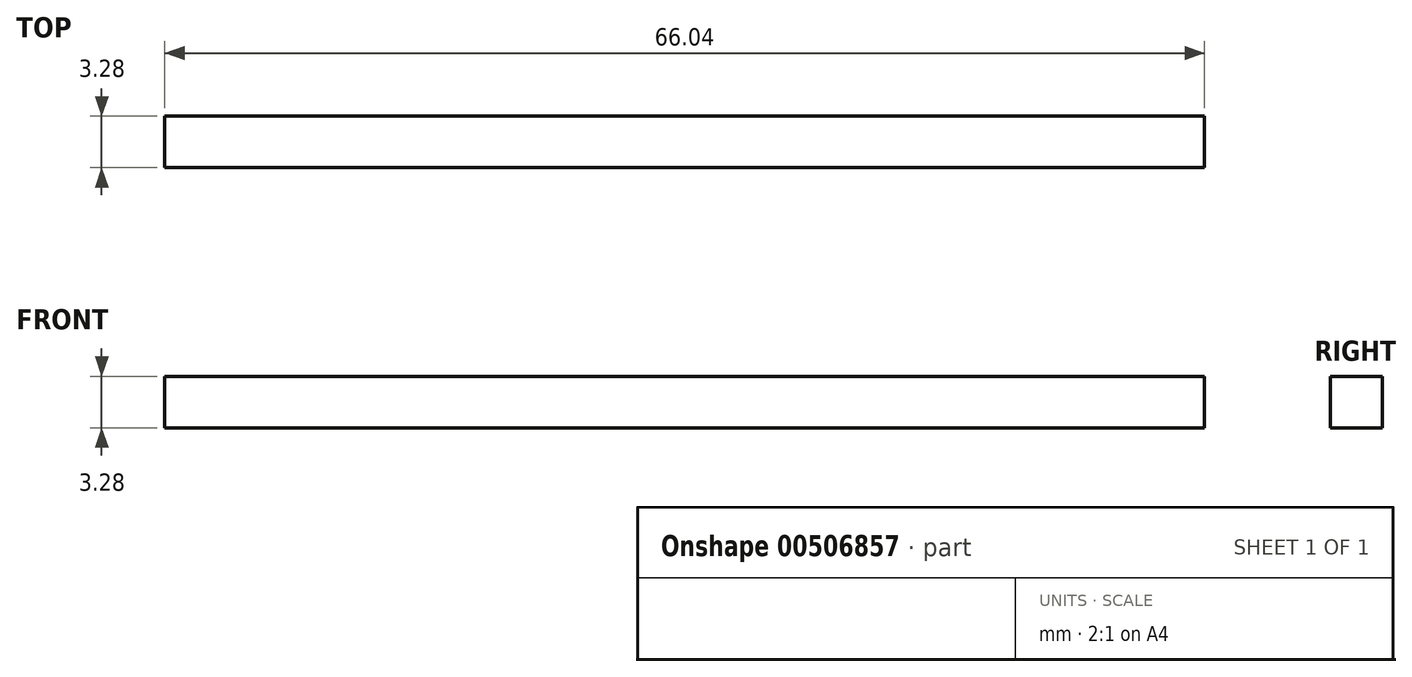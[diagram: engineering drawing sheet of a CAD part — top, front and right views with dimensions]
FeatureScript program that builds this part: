
annotation { "Feature Type Name" : "Feature", "Feature Type Description" : "" }
export const myFeature = defineFeature(function(context is Context, id is Id, definition is map)
    precondition{}
    {
        {
            var Q0;
            Q0=qCreatedBy(makeId("Top.planeOp"),FACE);
            var sketch = newSketch(context, id + "F0", { "sketchPlane" : qUnion([Q0])});
            skLineSegment(sketch, "E0.bottom", {"start": v(-66.71, -10.6) * mm, "end": v(-0.67, -10.6) * mm});
            skLineSegment(sketch, "E0.top", {"start": v(-66.71, -13.89) * mm, "end": v(-0.67, -13.89) * mm});
            skLineSegment(sketch, "E0.left", {"start": v(-66.71, -10.6) * mm, "end": v(-66.71, -13.89) * mm});
            skLineSegment(sketch, "E0.right", {"start": v(-0.67, -10.6) * mm, "end": v(-0.67, -13.89) * mm});
            skSolve(sketch);
        }
        {
            var Q0;
            Q0=makeQuery(id+"F0.imprint","IMPRINT",FACE,{"disambiguationData":[TD([[makeQuery(id+"F0.imprint","IMPRINT",EDGE,{"derivedFrom":sQuery(id+"F0.wireOp",EDGE,"E0.bottom")}),-1.0]])]});
            extrude(context, id + "F1", {"entities" : qUnion([Q0]), "depth" : 3.28 * mm, "offsetDistance" : 25.4 * mm});
        }
    });
